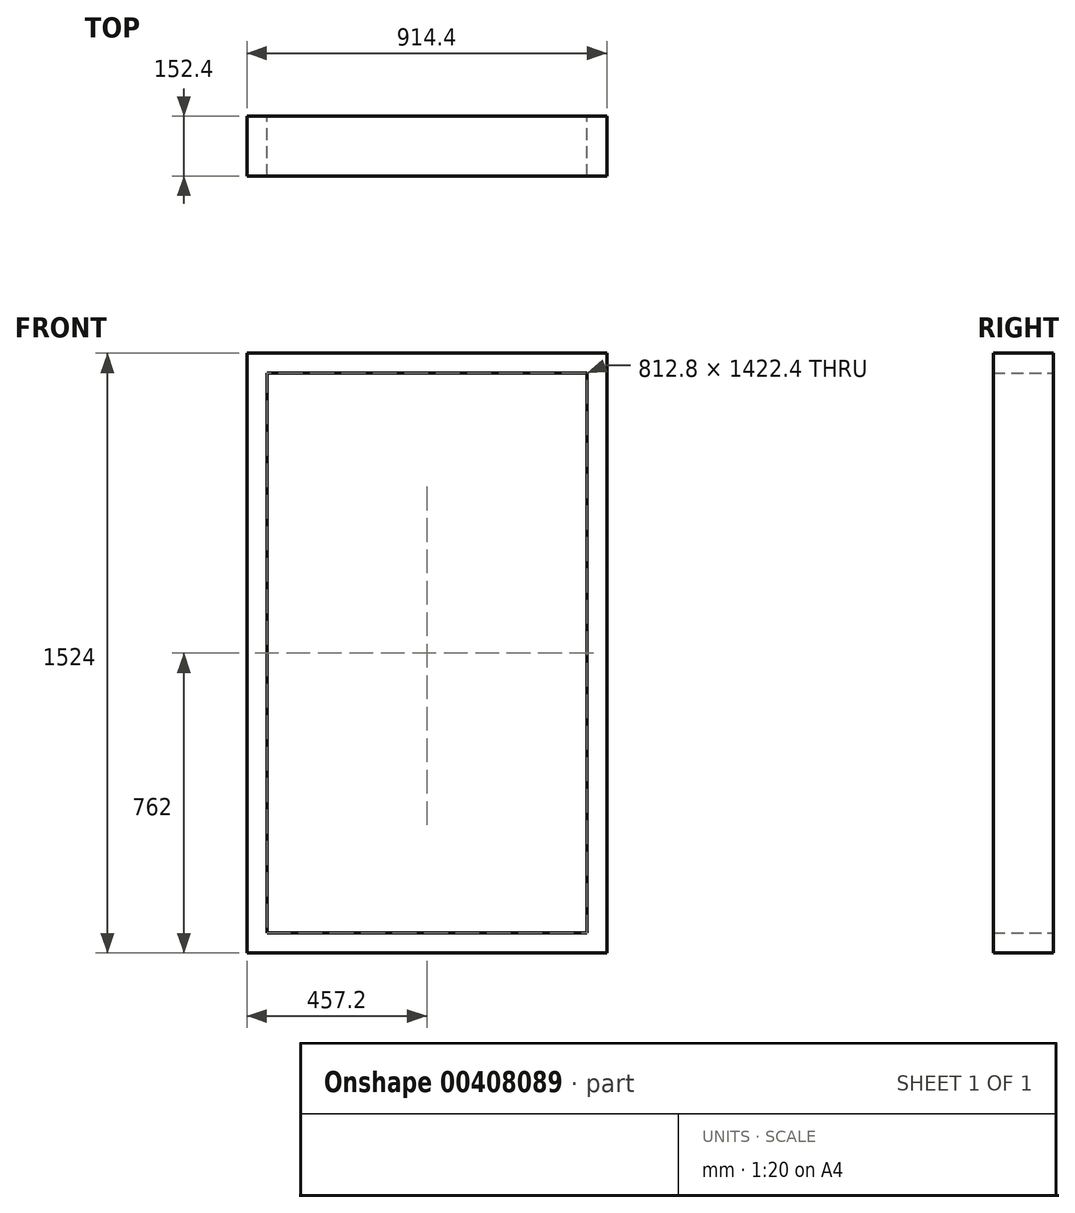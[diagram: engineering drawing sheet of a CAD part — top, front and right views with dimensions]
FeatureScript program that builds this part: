
annotation { "Feature Type Name" : "Feature", "Feature Type Description" : "" }
export const myFeature = defineFeature(function(context is Context, id is Id, definition is map)
    precondition{}
    {
        {
            var Q0;
            Q0=qCreatedBy(makeId("Front.planeOp"),FACE);
            var sketch = newSketch(context, id + "F0", { "sketchPlane" : qUnion([Q0])});
            skLineSegment(sketch, "E0.bottom", {"start": v(457.2, -762) * mm, "end": v(-457.2, -762) * mm});
            skLineSegment(sketch, "E0.top", {"start": v(457.2, 762) * mm, "end": v(-457.2, 762) * mm});
            skLineSegment(sketch, "E0.left", {"start": v(457.2, -762) * mm, "end": v(457.2, 762) * mm});
            skLineSegment(sketch, "E0.right", {"start": v(-457.2, -762) * mm, "end": v(-457.2, 762) * mm});
            skPoint(sketch, "E0.middle", {"position": v(0, 0) * mm});
            skSolve(sketch);
        }
        {
            var Q0;
            Q0 = qSketchRegion(id + "F0", true);
            extrude(context, id + "F1", {"entities" : qUnion([Q0]), "depth" : 152.4 * mm});
        }
        {
            var Q0;
            Q0=makeQuery(id+"F1.opExtrude","CAP_FACE",FACE,{"disambiguationData":[OSD([sQuery(id+"F0.wireOp",EDGE,"E0.bottom"),sQuery(id+"F0.wireOp",EDGE,"E0.top"),sQuery(id+"F0.wireOp",EDGE,"E0.left"),sQuery(id+"F0.wireOp",EDGE,"E0.right")])],"isStart":false});
            var Q1;
            Q1=makeQuery(id+"F1.opExtrude","CAP_FACE",FACE,{"disambiguationData":[OSD([sQuery(id+"F0.wireOp",EDGE,"E0.bottom"),sQuery(id+"F0.wireOp",EDGE,"E0.top"),sQuery(id+"F0.wireOp",EDGE,"E0.left"),sQuery(id+"F0.wireOp",EDGE,"E0.right")])],"isStart":true});
            var Q2;
            Q2=makeQuery(id+"F1.opExtrude","SWEPT_BODY",BODY,{"disambiguationData":[OSD([sQuery(id+"F0.wireOp",EDGE,"E0.bottom"),sQuery(id+"F0.wireOp",EDGE,"E0.top"),sQuery(id+"F0.wireOp",EDGE,"E0.left"),sQuery(id+"F0.wireOp",EDGE,"E0.right")])]});
            shell(context, id + "F2", {"entities" : qUnion([Q0, Q1]), "parts" : qUnion([Q2]), "thickness" : 50.8 * mm});
        }
    });
